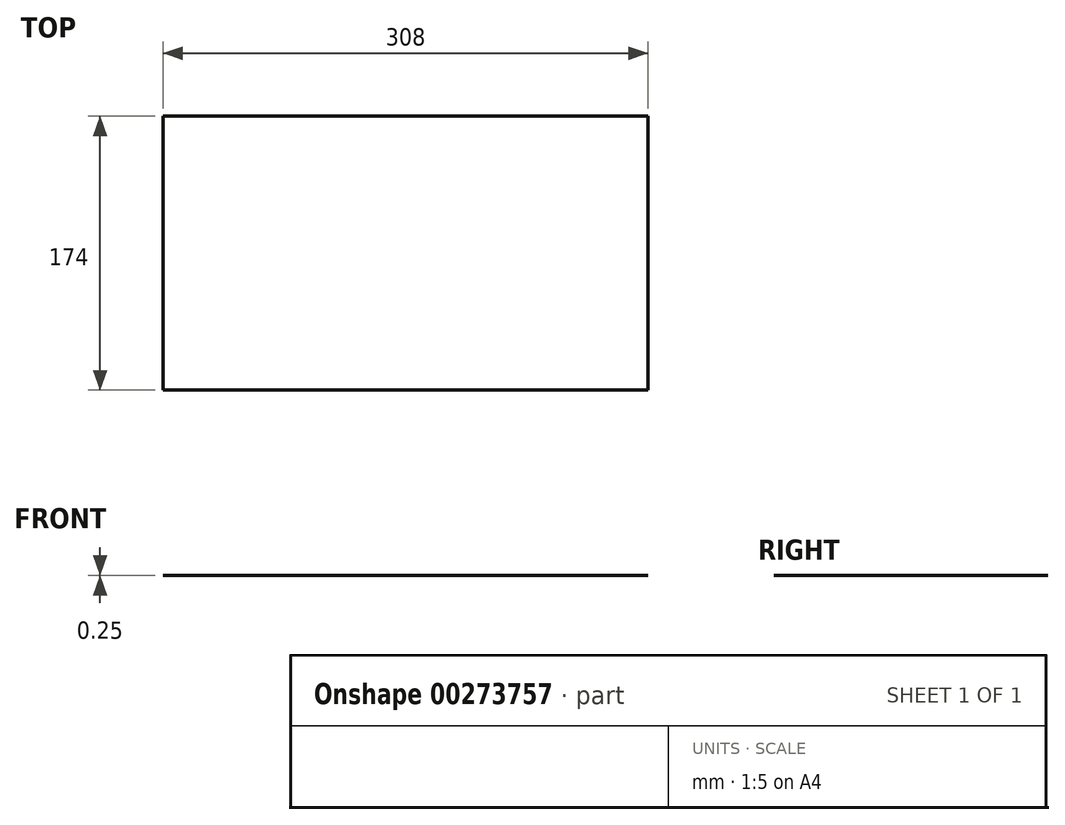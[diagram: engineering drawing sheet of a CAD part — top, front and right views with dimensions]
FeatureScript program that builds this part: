
annotation { "Feature Type Name" : "Feature", "Feature Type Description" : "" }
export const myFeature = defineFeature(function(context is Context, id is Id, definition is map)
    precondition{}
    {
        {
            var Q0;
            Q0=qCreatedBy(makeId("Top.planeOp"),FACE);
            var sketch = newSketch(context, id + "F0", { "sketchPlane" : qUnion([Q0])});
            skLineSegment(sketch, "E0.bottom", {"start": v(154, 87) * mm, "end": v(-154, 87) * mm});
            skLineSegment(sketch, "E0.top", {"start": v(154, -87) * mm, "end": v(-154, -87) * mm});
            skLineSegment(sketch, "E0.left", {"start": v(154, 87) * mm, "end": v(154, -87) * mm});
            skLineSegment(sketch, "E0.right", {"start": v(-154, 87) * mm, "end": v(-154, -87) * mm});
            skPoint(sketch, "E0.middle", {"position": v(0, 0) * mm});
            skSolve(sketch);
        }
        {
            var Q0;
            Q0=makeQuery(id+"F0.imprint","IMPRINT",FACE,{"disambiguationData":[TD([[makeQuery(id+"F0.imprint","IMPRINT",EDGE,{"derivedFrom":sQuery(id+"F0.wireOp",EDGE,"E0.bottom")}),1.0]])]});
            extrude(context, id + "F1", {"entities" : qUnion([Q0]), "depth" : .25 * mm});
        }
    });
